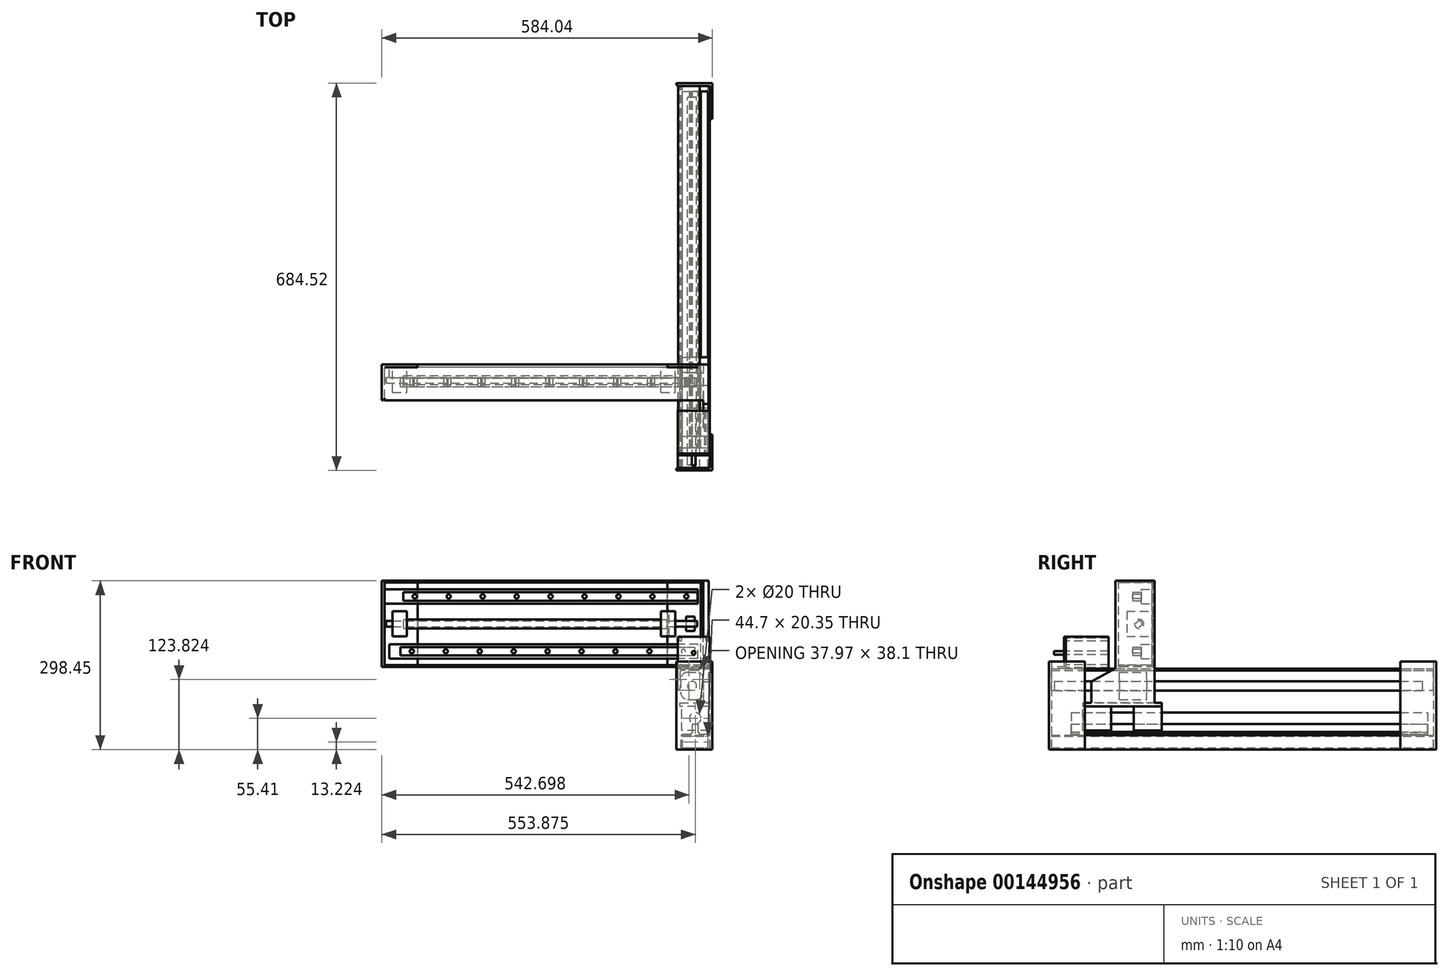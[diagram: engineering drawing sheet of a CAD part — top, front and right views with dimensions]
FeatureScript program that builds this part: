
annotation { "Feature Type Name" : "Feature", "Feature Type Description" : "" }
export const myFeature = defineFeature(function(context is Context, id is Id, definition is map)
    precondition{}
    {
        {
            var Q0;
            Q0=qCreatedBy(makeId("Front.planeOp"),FACE);
            var sketch = newSketch(context, id + "F0", { "sketchPlane" : qUnion([Q0])});
            skLineSegment(sketch, "E0.bottom", {"start": v(200.9, 0) * mm, "end": v(247.7, 0) * mm});
            skLineSegment(sketch, "E0.top", {"start": v(200.9, 25.4) * mm, "end": v(247.7, 25.4) * mm});
            skLineSegment(sketch, "E0.left", {"start": v(198.9, 2) * mm, "end": v(198.9, 23.4) * mm});
            skLineSegment(sketch, "E0.right", {"start": v(249.7, 2) * mm, "end": v(249.7, 23.4) * mm});
            skPoint(sketch, "E1.visualSharp", {"position": v(198.9, 25.4) * mm});
            skArc(sketch, "E1.filletArc", {"start": v(200.9, 25.4) * mm, "mid": v(199.48, 24.81) * mm, "end": v(198.9, 23.4) * mm});
            skPoint(sketch, "E2.visualSharp", {"position": v(198.9, 0) * mm});
            skArc(sketch, "E2.filletArc", {"start": v(198.9, 2) * mm, "mid": v(199.48, 0.59) * mm, "end": v(200.9, 0) * mm});
            skPoint(sketch, "E3.visualSharp", {"position": v(249.7, 25.4) * mm});
            skArc(sketch, "E3.filletArc", {"start": v(249.7, 23.4) * mm, "mid": v(249.1, 24.81) * mm, "end": v(247.7, 25.4) * mm});
            skPoint(sketch, "E4.visualSharp", {"position": v(249.7, 0) * mm});
            skArc(sketch, "E4.filletArc", {"start": v(247.7, 0) * mm, "mid": v(249.1, 0.59) * mm, "end": v(249.7, 2) * mm});
            skLineSegment(sketch, "E5.bottom", {"start": v(201.94, 3.05) * mm, "end": v(246.65, 3.05) * mm});
            skLineSegment(sketch, "E5.top", {"start": v(201.94, 23.4) * mm, "end": v(246.65, 23.4) * mm});
            skLineSegment(sketch, "E5.left", {"start": v(201.94, 3.05) * mm, "end": v(201.94, 23.4) * mm});
            skLineSegment(sketch, "E5.right", {"start": v(246.65, 3.05) * mm, "end": v(246.65, 23.4) * mm});
            skSolve(sketch);
        }
        {
            var Q0;
            Q0=makeQuery(id+"F0.imprint","IMPRINT",FACE,{"disambiguationData":[TD([[makeQuery(id+"F0.imprint","IMPRINT",EDGE,{"derivedFrom":sQuery(id+"F0.wireOp",EDGE,"E0.bottom")}),1.0]])]});
            extrude(context, id + "F1", {"entities" : qUnion([Q0]), "depth" : 675 * mm});
        }
        {
            var Q0;
            Q0=makeQuery(id+"F1.opExtrude","SWEPT_FACE",FACE,{"disambiguationData":[OSD([sQuery(id+"F0.wireOp",EDGE,"E5.bottom")])]});
            var sketch = newSketch(context, id + "F2", { "sketchPlane" : qUnion([Q0])});
            skLineSegment(sketch, "E6", {"start": v(193.96, -675) * mm, "end": v(249.7, -675) * mm});
            skLineSegment(sketch, "E7", {"start": v(249.7, -675) * mm, "end": v(249.7, -619.26) * mm});
            skLineSegment(sketch, "E8", {"start": v(252.7, -616.26) * mm, "end": v(254.46, -616.26) * mm});
            skLineSegment(sketch, "E9", {"start": v(254.46, -616.26) * mm, "end": v(254.46, -679.76) * mm});
            skLineSegment(sketch, "E10", {"start": v(254.46, -679.76) * mm, "end": v(190.96, -679.76) * mm});
            skLineSegment(sketch, "E11", {"start": v(190.96, -679.76) * mm, "end": v(190.96, -678) * mm});
            skPoint(sketch, "E12.visualSharp", {"position": v(190.96, -675) * mm});
            skArc(sketch, "E12.filletArc", {"start": v(193.96, -675) * mm, "mid": v(191.84, -675.88) * mm, "end": v(190.96, -678) * mm});
            skPoint(sketch, "E13.visualSharp", {"position": v(249.7, -616.26) * mm});
            skArc(sketch, "E13.filletArc", {"start": v(252.7, -616.26) * mm, "mid": v(250.57, -617.14) * mm, "end": v(249.7, -619.26) * mm});
            skSolve(sketch);
        }
        {
            var Q0;
            {var subQ0=sQuery(id+"F2.wireOp",EDGE,"E7");Q0=makeQuery(id+"F2.imprint","IMPRINT",FACE,{"disambiguationData":[TD([[makeQuery(id+"F2.imprint","IMPRINT",EDGE,{"derivedFrom":subQ0}),-1.0]])]});}
            extrude(context, id + "F3", {"entities" : qUnion([Q0]), "depth" : 152.4 * mm, "hasSecondDirection" : true, "secondDirectionOppositeDirection" : true, "secondDirectionDepth" : 3.05 * mm});
        }
        {
            var Q0;
            Q0=makeQuery(id+"F1.opExtrude","CAP_FACE",FACE,{"disambiguationData":[OSD([sQuery(id+"F0.wireOp",EDGE,"E0.bottom"),sQuery(id+"F0.wireOp",EDGE,"E0.top"),sQuery(id+"F0.wireOp",EDGE,"E0.left"),sQuery(id+"F0.wireOp",EDGE,"E0.right"),sQuery(id+"F0.wireOp",EDGE,"E1.filletArc"),sQuery(id+"F0.wireOp",EDGE,"E2.filletArc"),sQuery(id+"F0.wireOp",EDGE,"E3.filletArc"),sQuery(id+"F0.wireOp",EDGE,"E4.filletArc"),sQuery(id+"F0.wireOp",EDGE,"E5.bottom"),sQuery(id+"F0.wireOp",EDGE,"E5.top"),sQuery(id+"F0.wireOp",EDGE,"E5.left"),sQuery(id+"F0.wireOp",EDGE,"E5.right")])],"isStart":true});
            var sketch = newSketch(context, id + "F4", { "sketchPlane" : qUnion([Q0])});
            skLineSegment(sketch, "E14", {"start": v(-246.8, 25.4) * mm, "end": v(-201.8, 25.4) * mm});
            skLineSegment(sketch, "E15", {"start": v(-201.8, 25.4) * mm, "end": v(-201.8, 27.4) * mm});
            skLineSegment(sketch, "E16", {"start": v(-201.8, 27.4) * mm, "end": v(-216.8, 27.4) * mm});
            skLineSegment(sketch, "E17", {"start": v(-216.8, 27.4) * mm, "end": v(-219.31, 30.72) * mm});
            skLineSegment(sketch, "E18", {"start": v(-219.31, 30.72) * mm, "end": v(-219.31, 45.4) * mm});
            skLineSegment(sketch, "E19", {"start": v(-219.31, 45.4) * mm, "end": v(-229.31, 45.4) * mm});
            skLineSegment(sketch, "E20", {"start": v(-229.31, 45.4) * mm, "end": v(-229.31, 30.97) * mm});
            skLineSegment(sketch, "E21", {"start": v(-229.31, 30.97) * mm, "end": v(-231.8, 27.4) * mm});
            skLineSegment(sketch, "E22", {"start": v(-231.8, 27.4) * mm, "end": v(-246.8, 27.4) * mm});
            skLineSegment(sketch, "E23", {"start": v(-246.8, 27.4) * mm, "end": v(-246.8, 25.4) * mm});
            skCircle(sketch, "E24", {"center": v(-224.3, 55.41) * mm, "radius": 10 * mm});
            skSolve(sketch);
        }
        {
            var Q0;
            Q0=makeQuery(id+"F4.imprint","IMPRINT",FACE,{"disambiguationData":[TD([[makeQuery(id+"F4.imprint","IMPRINT",EDGE,{"derivedFrom":sQuery(id+"F4.wireOp",EDGE,"E24")}),1.0]])]});
            var Q1;
            Q1=makeQuery(id+"F4.imprint","IMPRINT",FACE,{"disambiguationData":[TD([[makeQuery(id+"F4.imprint","IMPRINT",EDGE,{"derivedFrom":sQuery(id+"F4.wireOp",EDGE,"E14")}),-1.0]])]});
            extrude(context, id + "F5", {"entities" : qUnion([Q0, Q1]), "oppositeDirection" : true, "depth" : 640 * mm, "hasSecondDirection" : true, "secondDirectionOppositeDirection" : true, "secondDirectionDepth" : 10 * mm});
        }
        {
            var Q0;
            Q0=makeQuery(id+"F1.opExtrude","SWEPT_FACE",FACE,{"disambiguationData":[OSD([sQuery(id+"F0.wireOp",EDGE,"E5.bottom")])]});
            var sketch = newSketch(context, id + "F6", { "sketchPlane" : qUnion([Q0])});
            skLineSegment(sketch, "E25", {"start": v(194, 0) * mm, "end": v(249.7, 0) * mm});
            skLineSegment(sketch, "E26", {"start": v(249.7, 0) * mm, "end": v(249.7, -55.74) * mm});
            skLineSegment(sketch, "E27", {"start": v(252.7, -58.74) * mm, "end": v(254.46, -58.74) * mm});
            skLineSegment(sketch, "E28", {"start": v(254.46, -58.74) * mm, "end": v(254.46, 4.76) * mm});
            skLineSegment(sketch, "E29", {"start": v(254.46, 4.76) * mm, "end": v(190.96, 4.76) * mm});
            skLineSegment(sketch, "E30", {"start": v(190.96, 4.76) * mm, "end": v(191, 2.93) * mm});
            skPoint(sketch, "E31.visualSharp", {"position": v(191.08, 0) * mm});
            skArc(sketch, "E31.filletArc", {"start": v(191, 2.93) * mm, "mid": v(191.9, 0.85) * mm, "end": v(194, 0) * mm});
            skPoint(sketch, "E32.visualSharp", {"position": v(249.7, -58.74) * mm});
            skArc(sketch, "E32.filletArc", {"start": v(249.7, -55.74) * mm, "mid": v(250.57, -57.86) * mm, "end": v(252.7, -58.74) * mm});
            skSolve(sketch);
        }
        {
            var Q0;
            {var subQ0=sQuery(id+"F6.wireOp",EDGE,"E26");Q0=makeQuery(id+"F6.imprint","IMPRINT",FACE,{"disambiguationData":[TD([[makeQuery(id+"F6.imprint","IMPRINT",EDGE,{"derivedFrom":subQ0}),1.0]])]});}
            extrude(context, id + "F7", {"entities" : qUnion([Q0]), "depth" : 152.4 * mm, "hasSecondDirection" : true, "secondDirectionOppositeDirection" : true, "secondDirectionDepth" : 3.05 * mm});
        }
        {
            var Q0;
            Q0=makeQuery(id+"F7.opExtrude","SWEPT_FACE",FACE,{"disambiguationData":[OSD([sQuery(id+"F6.wireOp",EDGE,"E25")])]});
            var sketch = newSketch(context, id + "F8", { "sketchPlane" : qUnion([Q0])});
            skLineSegment(sketch, "E33", {"start": v(194, 142.88) * mm, "end": v(232.1, 142.88) * mm});
            skLineSegment(sketch, "E34", {"start": v(232.1, 142.88) * mm, "end": v(232.1, 142.7) * mm});
            skLineSegment(sketch, "E35", {"start": v(229.1, 139.7) * mm, "end": v(200.3, 139.7) * mm});
            skLineSegment(sketch, "E36", {"start": v(194.13, 104.77) * mm, "end": v(194.13, 142.88) * mm});
            skPoint(sketch, "E37.visualSharp", {"position": v(232.1, 139.7) * mm});
            skArc(sketch, "E37.filletArc", {"start": v(229.1, 139.7) * mm, "mid": v(231.22, 140.58) * mm, "end": v(232.1, 142.7) * mm});
            skLineSegment(sketch, "E38", {"start": v(197.3, 136.7) * mm, "end": v(197.3, 107.77) * mm});
            skLineSegment(sketch, "E39", {"start": v(194.24, 104.77) * mm, "end": v(194.13, 104.77) * mm});
            skPoint(sketch, "E40.visualSharp", {"position": v(197.3, 139.7) * mm});
            skArc(sketch, "E40.filletArc", {"start": v(200.3, 139.7) * mm, "mid": v(198.19, 138.82) * mm, "end": v(197.3, 136.7) * mm});
            skPoint(sketch, "E41.visualSharp", {"position": v(197.3, 104.7) * mm});
            skArc(sketch, "E41.filletArc", {"start": v(194.24, 104.77) * mm, "mid": v(196.4, 105.63) * mm, "end": v(197.3, 107.77) * mm});
            skSolve(sketch);
        }
        {
            var Q0;
            Q0=makeQuery(id+"F8.imprint","IMPRINT",FACE,{"disambiguationData":[TD([[makeQuery(id+"F8.imprint","IMPRINT",EDGE,{"derivedFrom":sQuery(id+"F8.wireOp",EDGE,"E33")}),-1.0]])]});
            extrude(context, id + "F9", {"entities" : qUnion([Q0]), "operationType" : NewBodyOperationType.ADD, "depth" : 675 * mm});
        }
        {
            var Q0;
            Q0=makeQuery(id+"F5.opExtrude","CAP_FACE",FACE,{"disambiguationData":[OSD([sQuery(id+"F4.wireOp",EDGE,"E24")])],"isStart":true});
            var sketch = newSketch(context, id + "F10", { "sketchPlane" : qUnion([Q0])});
            skLineSegment(sketch, "E42.bottom", {"start": v(-248.3, 33.48) * mm, "end": v(-200.3, 33.48) * mm});
            skLineSegment(sketch, "E42.top", {"start": v(-248.3, 76.2) * mm, "end": v(-200.3, 76.2) * mm});
            skLineSegment(sketch, "E42.left", {"start": v(-248.3, 33.48) * mm, "end": v(-248.3, 76.2) * mm});
            skLineSegment(sketch, "E42.right", {"start": v(-200.3, 33.48) * mm, "end": v(-200.3, 76.2) * mm});
            skLineSegment(sketch, "E43", {"start": v(-248.3, 76.2) * mm, "end": v(-197.5, 76.2) * mm});
            skLineSegment(sketch, "E44", {"start": v(-197.5, 76.2) * mm, "end": v(-197.5, 82.55) * mm});
            skLineSegment(sketch, "E45", {"start": v(-197.5, 82.55) * mm, "end": v(-248.3, 82.55) * mm});
            skLineSegment(sketch, "E46", {"start": v(-248.3, 82.55) * mm, "end": v(-248.3, 76.2) * mm});
            skCircle(sketch, "E47", {"center": v(-218.77, 112.55) * mm, "radius": 8 * mm});
            skLineSegment(sketch, "E48.bottom", {"start": v(-210.77, 136.55) * mm, "end": v(-226.77, 136.55) * mm});
            skLineSegment(sketch, "E48.top", {"start": v(-210.77, 88.55) * mm, "end": v(-226.77, 88.55) * mm});
            skLineSegment(sketch, "E48.left", {"start": v(-198.77, 124.55) * mm, "end": v(-198.77, 100.55) * mm});
            skLineSegment(sketch, "E48.right", {"start": v(-238.77, 124.55) * mm, "end": v(-238.77, 100.55) * mm});
            skPoint(sketch, "E49.visualSharp", {"position": v(-198.77, 136.55) * mm});
            skArc(sketch, "E49.filletArc", {"start": v(-198.77, 124.55) * mm, "mid": v(-202.28, 133.03) * mm, "end": v(-210.77, 136.55) * mm});
            skPoint(sketch, "E50.visualSharp", {"position": v(-198.77, 88.55) * mm});
            skArc(sketch, "E50.filletArc", {"start": v(-210.77, 88.55) * mm, "mid": v(-202.28, 92.06) * mm, "end": v(-198.77, 100.55) * mm});
            skPoint(sketch, "E51.visualSharp", {"position": v(-238.77, 88.55) * mm});
            skArc(sketch, "E51.filletArc", {"start": v(-238.77, 100.55) * mm, "mid": v(-235.26, 92.06) * mm, "end": v(-226.77, 88.55) * mm});
            skPoint(sketch, "E52.visualSharp", {"position": v(-238.77, 136.55) * mm});
            skArc(sketch, "E52.filletArc", {"start": v(-226.77, 136.55) * mm, "mid": v(-235.26, 133.03) * mm, "end": v(-238.77, 124.55) * mm});
            skSolve(sketch);
        }
        {
            var Q0;
            Q0=makeQuery(id+"F10.imprint","IMPRINT",FACE,{"disambiguationData":[TD([[makeQuery(id+"F10.imprint","IMPRINT",EDGE,{"derivedFrom":sQuery(id+"F10.wireOp",EDGE,"E42.bottom")}),1.0]])]});
            extrude(context, id + "F11", {"entities" : qUnion([Q0]), "oppositeDirection" : true, "depth" : 520 * mm, "hasSecondDirection" : true, "secondDirectionOppositeDirection" : true, "secondDirectionDepth" : 470 * mm});
        }
        {
            var Q0;
            Q0=makeQuery(id+"F11.opExtrude","CAP_FACE",FACE,{"disambiguationData":[OSD([sQuery(id+"F4.wireOp",EDGE,"E24"),sQuery(id+"F10.wireOp",EDGE,"E42.bottom"),sQuery(id+"F10.wireOp",EDGE,"E42.left"),sQuery(id+"F10.wireOp",EDGE,"E42.right"),sQuery(id+"F10.wireOp",EDGE,"E43")])],"isStart":true});
            extrude(context, id + "F12", {"entities" : qUnion([Q0]), "oppositeDirection" : true, "depth" : 139.7 * mm, "hasSecondDirection" : true, "secondDirectionOppositeDirection" : true, "secondDirectionDepth" : 89.7 * mm});
        }
        {
            var Q0;
            {var subQ0=sQuery(id+"F10.wireOp",EDGE,"E44");Q0=makeQuery(id+"F10.imprint","IMPRINT",FACE,{"disambiguationData":[TD([[makeQuery(id+"F10.imprint","IMPRINT",EDGE,{"derivedFrom":subQ0}),1.0]])]});}
            extrude(context, id + "F13", {"entities" : qUnion([Q0]), "oppositeDirection" : true, "depth" : 609.7 * mm, "hasSecondDirection" : true, "secondDirectionOppositeDirection" : true, "secondDirectionDepth" : 470 * mm});
        }
        {
            var Q0;
            Q0=makeQuery(id+"F13.opExtrude","SWEPT_FACE",FACE,{"disambiguationData":[OSD([sQuery(id+"F10.wireOp",EDGE,"E45")])]});
            var sketch = newSketch(context, id + "F14", { "sketchPlane" : qUnion([Q0])});
            skLineSegment(sketch, "E53.bottom", {"start": v(248.3, -492.7) * mm, "end": v(238.77, -492.7) * mm});
            skLineSegment(sketch, "E53.top", {"start": v(248.3, -604.7) * mm, "end": v(238.77, -604.7) * mm});
            skLineSegment(sketch, "E53.left", {"start": v(248.3, -492.7) * mm, "end": v(248.3, -604.7) * mm});
            skLineSegment(sketch, "E53.right", {"start": v(238.77, -492.7) * mm, "end": v(238.77, -604.7) * mm});
            skSolve(sketch);
        }
        {
            var Q0;
            Q0=makeQuery(id+"F14.imprint","IMPRINT",FACE,{"disambiguationData":[TD([[makeQuery(id+"F14.imprint","IMPRINT",EDGE,{"derivedFrom":sQuery(id+"F14.wireOp",EDGE,"E53.bottom")}),1.0]])]});
            extrude(context, id + "F15", {"entities" : qUnion([Q0]), "operationType" : NewBodyOperationType.ADD, "depth" : 215.9 * mm});
        }
        {
            var Q0;
            Q0=makeQuery(id+"F10.imprint","IMPRINT",FACE,{"disambiguationData":[TD([[makeQuery(id+"F10.imprint","IMPRINT",EDGE,{"derivedFrom":sQuery(id+"F10.wireOp",EDGE,"E47")}),1.0]])]});
            extrude(context, id + "F16", {"entities" : qUnion([Q0]), "oppositeDirection" : true, "depth" : 660 * mm, "hasSecondDirection" : true, "secondDirectionOppositeDirection" : true, "secondDirectionDepth" : 10 * mm});
        }
        {
            var Q0;
            Q0=makeQuery(id+"F10.imprint","IMPRINT",FACE,{"disambiguationData":[TD([[makeQuery(id+"F10.imprint","IMPRINT",EDGE,{"derivedFrom":sQuery(id+"F10.wireOp",EDGE,"E47")}),-1.0]])]});
            extrude(context, id + "F17", {"entities" : qUnion([Q0]), "oppositeDirection" : true, "depth" : 545 * mm, "hasSecondDirection" : true, "secondDirectionOppositeDirection" : true, "secondDirectionDepth" : 497 * mm});
        }
        {
            var Q0;
            Q0=makeQuery(id+"F15.boolean.opBoolean","MERGE",FACE,{"derivedFrom":[makeQuery(id+"F13.opExtrude","SWEPT_FACE",FACE,{"disambiguationData":[OSD([sQuery(id+"F10.wireOp",EDGE,"E46")])]}),makeQuery(id+"F15.opExtrude","SWEPT_FACE",FACE,{"disambiguationData":[OSD([sQuery(id+"F14.wireOp",EDGE,"E53.left")])]})]});
            var sketch = newSketch(context, id + "F18", { "sketchPlane" : qUnion([Q0])});
            skLineSegment(sketch, "E54", {"start": v(-604.7, 119.94) * mm, "end": v(-562.4, 143.7) * mm});
            skLineSegment(sketch, "E55", {"start": v(-562.4, 143.7) * mm, "end": v(-562.4, 298.45) * mm});
            skLineSegment(sketch, "E56", {"start": v(-562.4, 298.45) * mm, "end": v(-604.7, 298.45) * mm});
            skLineSegment(sketch, "E57", {"start": v(-604.7, 298.45) * mm, "end": v(-604.7, 119.94) * mm});
            skSolve(sketch);
        }
        {
            var Q0;
            Q0 = qSketchRegion(id + "F18", true);
            extrude(context, id + "F19", {"entities" : qUnion([Q0]), "operationType" : NewBodyOperationType.REMOVE, "oppositeDirection" : true, "depth" : 9.53 * mm});
        }
        {
            var Q0;
            Q0=makeQuery(id+"F9.opExtrude","SWEPT_FACE",FACE,{"disambiguationData":[OSD([sQuery(id+"F8.wireOp",EDGE,"E33")])]});
            var sketch = newSketch(context, id + "F20", { "sketchPlane" : qUnion([Q0])});
            skLineSegment(sketch, "E58.bottom", {"start": v(193.3, -650) * mm, "end": v(249.7, -650) * mm});
            skLineSegment(sketch, "E58.top", {"start": v(193.3, -675) * mm, "end": v(249.7, -675) * mm});
            skLineSegment(sketch, "E58.left", {"start": v(193.3, -650) * mm, "end": v(193.3, -675) * mm});
            skLineSegment(sketch, "E58.right", {"start": v(249.7, -650) * mm, "end": v(249.7, -675) * mm});
            skSolve(sketch);
        }
        {
            var Q0;
            Q0 = qSketchRegion(id + "F20", true);
            extrude(context, id + "F21", {"entities" : qUnion([Q0]), "depth" : 3.17 * mm});
        }
        {
            var Q0;
            Q0=makeQuery(id+"F21.opExtrude","CAP_FACE",FACE,{"disambiguationData":[OSD([sQuery(id+"F20.wireOp",EDGE,"E58.bottom"),sQuery(id+"F20.wireOp",EDGE,"E58.top"),sQuery(id+"F20.wireOp",EDGE,"E58.left"),sQuery(id+"F20.wireOp",EDGE,"E58.right")])],"isStart":false});
            var sketch = newSketch(context, id + "F22", { "sketchPlane" : qUnion([Q0])});
            skLineSegment(sketch, "E59.bottom", {"start": v(193.3, -650) * mm, "end": v(249.7, -650) * mm});
            skLineSegment(sketch, "E59.top", {"start": v(193.3, -653.18) * mm, "end": v(249.7, -653.18) * mm});
            skLineSegment(sketch, "E59.left", {"start": v(193.3, -650) * mm, "end": v(193.3, -653.18) * mm});
            skLineSegment(sketch, "E59.right", {"start": v(249.7, -650) * mm, "end": v(249.7, -653.18) * mm});
            skSolve(sketch);
        }
        {
            var Q0;
            Q0 = qSketchRegion(id + "F22", true);
            extrude(context, id + "F23", {"entities" : qUnion([Q0]), "depth" : 53.23 * mm});
        }
        {
            var Q0;
            Q0=makeQuery(id+"F23.opExtrude","SWEPT_FACE",FACE,{"disambiguationData":[OSD([sQuery(id+"F22.wireOp",EDGE,"E59.bottom")])]});
            var sketch = newSketch(context, id + "F24", { "sketchPlane" : qUnion([Q0])});
            skCircle(sketch, "E60", {"center": v(-221.5, 171.08) * mm, "radius": 3.17 * mm});
            skLineSegment(sketch, "E61.bottom", {"start": v(-244.7, 199.28) * mm, "end": v(-198.3, 199.28) * mm});
            skLineSegment(sketch, "E61.top", {"start": v(-244.7, 142.88) * mm, "end": v(-198.3, 142.88) * mm});
            skLineSegment(sketch, "E61.left", {"start": v(-249.7, 194.28) * mm, "end": v(-249.7, 147.88) * mm});
            skLineSegment(sketch, "E61.right", {"start": v(-193.3, 194.28) * mm, "end": v(-193.3, 147.88) * mm});
            skPoint(sketch, "E62.visualSharp", {"position": v(-249.7, 142.88) * mm});
            skArc(sketch, "E62.filletArc", {"start": v(-249.7, 147.88) * mm, "mid": v(-248.23, 144.34) * mm, "end": v(-244.7, 142.87) * mm});
            skPoint(sketch, "E63.visualSharp", {"position": v(-193.3, 142.88) * mm});
            skArc(sketch, "E63.filletArc", {"start": v(-198.3, 142.87) * mm, "mid": v(-194.76, 144.34) * mm, "end": v(-193.3, 147.88) * mm});
            skPoint(sketch, "E64.visualSharp", {"position": v(-249.7, 199.28) * mm});
            skArc(sketch, "E64.filletArc", {"start": v(-244.7, 199.28) * mm, "mid": v(-248.23, 197.81) * mm, "end": v(-249.7, 194.28) * mm});
            skPoint(sketch, "E65.visualSharp", {"position": v(-193.3, 199.28) * mm});
            skArc(sketch, "E65.filletArc", {"start": v(-193.3, 194.28) * mm, "mid": v(-194.76, 197.81) * mm, "end": v(-198.3, 199.28) * mm});
            skCircle(sketch, "E66", {"center": v(-197.92, 194.65) * mm, "radius": 2.55 * mm});
            skCircle(sketch, "E67", {"center": v(-197.92, 147.5) * mm, "radius": 2.55 * mm});
            skCircle(sketch, "E68", {"center": v(-245.06, 194.65) * mm, "radius": 2.55 * mm});
            skCircle(sketch, "E69", {"center": v(-243.2, 147.5) * mm, "radius": 2.55 * mm});
            skSolve(sketch);
        }
        {
            var Q0;
            Q0=makeQuery(id+"F24.imprint","IMPRINT",FACE,{"disambiguationData":[TD([[makeQuery(id+"F24.imprint","IMPRINT",EDGE,{"derivedFrom":sQuery(id+"F24.wireOp",EDGE,"E60")}),1.0]])]});
            extrude(context, id + "F25", {"entities" : qUnion([Q0]), "operationType" : NewBodyOperationType.ADD, "oppositeDirection" : true, "depth" : 21 * mm});
        }
        {
            var Q0;
            Q0 = qSketchRegion(id + "F24", true);
            extrude(context, id + "F26", {"entities" : qUnion([Q0]), "depth" : 76 * mm});
        }
        {
            var Q0;
            Q0=makeQuery(id+"F15.opExtrude","CAP_FACE",FACE,{"disambiguationData":[OSD([sQuery(id+"F14.wireOp",EDGE,"E53.bottom"),sQuery(id+"F14.wireOp",EDGE,"E53.top"),sQuery(id+"F14.wireOp",EDGE,"E53.left"),sQuery(id+"F14.wireOp",EDGE,"E53.right")])],"isStart":false});
            var sketch = newSketch(context, id + "F27", { "sketchPlane" : qUnion([Q0])});
            skLineSegment(sketch, "E70", {"start": v(238.77, -492.7) * mm, "end": v(238.77, -556.2) * mm});
            skLineSegment(sketch, "E71", {"start": v(238.77, -556.2) * mm, "end": v(236.76, -556.2) * mm});
            skLineSegment(sketch, "E72", {"start": v(234, -553.45) * mm, "end": v(234, -502.46) * mm});
            skLineSegment(sketch, "E73", {"start": v(229, -497.46) * mm, "end": v(178.2, -497.46) * mm});
            skLineSegment(sketch, "E74", {"start": v(175.27, -494.53) * mm, "end": v(175.27, -492.7) * mm});
            skLineSegment(sketch, "E75", {"start": v(175.27, -492.7) * mm, "end": v(238.77, -492.7) * mm});
            skPoint(sketch, "E76.visualSharp", {"position": v(234, -497.46) * mm});
            skArc(sketch, "E76.filletArc", {"start": v(234, -502.46) * mm, "mid": v(232.54, -498.93) * mm, "end": v(229, -497.46) * mm});
            skPoint(sketch, "E77.visualSharp", {"position": v(175.27, -497.46) * mm});
            skArc(sketch, "E77.filletArc", {"start": v(175.27, -494.53) * mm, "mid": v(176.13, -496.6) * mm, "end": v(178.2, -497.46) * mm});
            skPoint(sketch, "E78.visualSharp", {"position": v(234, -556.2) * mm});
            skArc(sketch, "E78.filletArc", {"start": v(234, -553.45) * mm, "mid": v(234.81, -555.4) * mm, "end": v(236.76, -556.2) * mm});
            skSolve(sketch);
        }
        {
            var Q0;
            Q0=makeQuery(id+"F27.imprint","IMPRINT",FACE,{"disambiguationData":[TD([[makeQuery(id+"F27.imprint","IMPRINT",EDGE,{"derivedFrom":sQuery(id+"F27.wireOp",EDGE,"E70")}),-1.0]])]});
            extrude(context, id + "F28", {"entities" : qUnion([Q0]), "operationType" : NewBodyOperationType.ADD, "oppositeDirection" : true, "depth" : 152.4 * mm});
        }
        {
            var Q0;
            Q0=makeQuery(id+"F28.opExtrude","SWEPT_FACE",FACE,{"disambiguationData":[OSD([sQuery(id+"F27.wireOp",EDGE,"E74")])]});
            var sketch = newSketch(context, id + "F29", { "sketchPlane" : qUnion([Q0])});
            skLineSegment(sketch, "E79.bottom", {"start": v(492.7, 298.45) * mm, "end": v(497.46, 298.45) * mm});
            skLineSegment(sketch, "E79.top", {"start": v(492.7, 146.05) * mm, "end": v(497.46, 146.05) * mm});
            skLineSegment(sketch, "E79.left", {"start": v(492.7, 298.45) * mm, "end": v(492.7, 146.05) * mm});
            skLineSegment(sketch, "E79.right", {"start": v(497.46, 298.45) * mm, "end": v(497.46, 146.05) * mm});
            skSolve(sketch);
        }
        {
            var Q0;
            Q0 = qSketchRegion(id + "F29", true);
            extrude(context, id + "F30", {"entities" : qUnion([Q0]), "operationType" : NewBodyOperationType.ADD, "depth" : 441.35 * mm});
        }
        {
            var Q0;
            Q0=makeQuery(id+"F30.boolean.opBoolean","MERGE",FACE,{"derivedFrom":[makeQuery(id+"F28.boolean.opBoolean","MERGE",FACE,{"derivedFrom":[makeQuery(id+"F15.opExtrude","CAP_FACE",FACE,{"disambiguationData":[OSD([sQuery(id+"F14.wireOp",EDGE,"E53.bottom"),sQuery(id+"F14.wireOp",EDGE,"E53.top"),sQuery(id+"F14.wireOp",EDGE,"E53.left"),sQuery(id+"F14.wireOp",EDGE,"E53.right")])],"isStart":false}),makeQuery(id+"F28.opExtrude","CAP_FACE",FACE,{"disambiguationData":[OSD([sQuery(id+"F27.wireOp",EDGE,"E70"),sQuery(id+"F27.wireOp",EDGE,"E71"),sQuery(id+"F27.wireOp",EDGE,"E72"),sQuery(id+"F27.wireOp",EDGE,"E73"),sQuery(id+"F27.wireOp",EDGE,"E74"),sQuery(id+"F27.wireOp",EDGE,"E75"),sQuery(id+"F27.wireOp",EDGE,"E76.filletArc"),sQuery(id+"F27.wireOp",EDGE,"E77.filletArc"),sQuery(id+"F27.wireOp",EDGE,"E78.filletArc")])],"isStart":true})]}),makeQuery(id+"F30.opExtrude","SWEPT_FACE",FACE,{"disambiguationData":[OSD([sQuery(id+"F29.wireOp",EDGE,"E79.bottom")])]})]});
            var sketch = newSketch(context, id + "F31", { "sketchPlane" : qUnion([Q0])});
            skLineSegment(sketch, "E80", {"start": v(-266.08, -492.7) * mm, "end": v(-329.58, -492.7) * mm});
            skLineSegment(sketch, "E81", {"start": v(-329.58, -492.7) * mm, "end": v(-329.58, -556.2) * mm});
            skLineSegment(sketch, "E82", {"start": v(-329.58, -556.2) * mm, "end": v(-329.16, -556.2) * mm});
            skLineSegment(sketch, "E83", {"start": v(-324.82, -551.86) * mm, "end": v(-324.82, -500.21) * mm});
            skLineSegment(sketch, "E84", {"start": v(-322.07, -497.46) * mm, "end": v(-270.07, -497.46) * mm});
            skLineSegment(sketch, "E85", {"start": v(-266.08, -493.47) * mm, "end": v(-266.08, -492.7) * mm});
            skPoint(sketch, "E86.visualSharp", {"position": v(-324.82, -497.46) * mm});
            skArc(sketch, "E86.filletArc", {"start": v(-322.07, -497.46) * mm, "mid": v(-324.01, -498.27) * mm, "end": v(-324.82, -500.21) * mm});
            skPoint(sketch, "E87.visualSharp", {"position": v(-266.08, -497.46) * mm});
            skArc(sketch, "E87.filletArc", {"start": v(-270.07, -497.46) * mm, "mid": v(-267.25, -496.3) * mm, "end": v(-266.08, -493.47) * mm});
            skPoint(sketch, "E88.visualSharp", {"position": v(-324.82, -556.2) * mm});
            skArc(sketch, "E88.filletArc", {"start": v(-329.16, -556.2) * mm, "mid": v(-326.09, -554.93) * mm, "end": v(-324.82, -551.86) * mm});
            skSolve(sketch);
        }
        {
            var Q0;
            Q0=makeQuery(id+"F31.imprint","IMPRINT",FACE,{"disambiguationData":[TD([[makeQuery(id+"F31.imprint","IMPRINT",EDGE,{"derivedFrom":sQuery(id+"F31.wireOp",EDGE,"E80")}),1.0]])]});
            extrude(context, id + "F32", {"entities" : qUnion([Q0]), "operationType" : NewBodyOperationType.ADD, "oppositeDirection" : true, "depth" : 152.4 * mm});
        }
        {
            var Q0;
            Q0=makeQuery(id+"F28.opExtrude","SWEPT_FACE",FACE,{"disambiguationData":[OSD([sQuery(id+"F27.wireOp",EDGE,"E73")])]});
            var sketch = newSketch(context, id + "F33", { "sketchPlane" : qUnion([Q0])});
            skLineSegment(sketch, "E89.bottom", {"start": v(234, 283.45) * mm, "end": v(-324.82, 283.45) * mm});
            skLineSegment(sketch, "E89.top", {"start": v(234, 258.05) * mm, "end": v(-324.82, 258.05) * mm});
            skLineSegment(sketch, "E89.left", {"start": v(234, 283.45) * mm, "end": v(234, 258.05) * mm});
            skLineSegment(sketch, "E89.right", {"start": v(-324.82, 283.45) * mm, "end": v(-324.82, 258.05) * mm});
            skLineSegment(sketch, "E90.bottom", {"start": v(233.5, 186.45) * mm, "end": v(-316.5, 186.45) * mm});
            skLineSegment(sketch, "E90.top", {"start": v(233.5, 161.05) * mm, "end": v(-316.5, 161.05) * mm});
            skLineSegment(sketch, "E90.left", {"start": v(233.5, 186.45) * mm, "end": v(233.5, 161.05) * mm});
            skLineSegment(sketch, "E90.right", {"start": v(-316.5, 186.45) * mm, "end": v(-316.5, 161.05) * mm});
            skSolve(sketch);
        }
        {
            var Q0;
            {var subQ0=sQuery(id+"F33.wireOp",EDGE,"E89.right");Q0=makeQuery(id+"F33.imprint","IMPRINT",FACE,{"disambiguationData":[TD([[makeQuery(id+"F33.imprint","IMPRINT",EDGE,{"derivedFrom":subQ0}),1.0]])]});}
            var Q1;
            {var subQ0=sQuery(id+"F33.wireOp",EDGE,"E89.bottom");var subQ1=sQuery(id+"F27.wireOp",EDGE,"E73");var subQ2=makeQuery(id+"F28.opExtrude","SWEPT_EDGE",EDGE,{"disambiguationData":[OSD([subQ1,sQuery(id+"F27.wireOp",EDGE,"E76.filletArc")])]});var subQ3=makeQuery(id+"F33.imprint","INTERSECT",VERTEX,{"derivedFrom":[subQ2,subQ0]});Q1=makeQuery(id+"F33.imprint","IMPRINT",FACE,{"disambiguationData":[TD([[makeQuery(id+"F33.imprint","IMPRINT",EDGE,{"disambiguationData":[TD([[subQ3,-1.0]])],"derivedFrom":subQ0}),1.0]])]});}
            var Q2;
            {var subQ0=sQuery(id+"F33.wireOp",EDGE,"E90.bottom");var subQ1=sQuery(id+"F27.wireOp",EDGE,"E73");var subQ2=makeQuery(id+"F28.opExtrude","SWEPT_EDGE",EDGE,{"disambiguationData":[OSD([subQ1,sQuery(id+"F27.wireOp",EDGE,"E76.filletArc")])]});var subQ3=makeQuery(id+"F33.imprint","INTERSECT",VERTEX,{"derivedFrom":[subQ2,subQ0]});Q2=makeQuery(id+"F33.imprint","IMPRINT",FACE,{"disambiguationData":[TD([[makeQuery(id+"F33.imprint","IMPRINT",EDGE,{"disambiguationData":[TD([[subQ3,-1.0]])],"derivedFrom":subQ0}),1.0]])]});}
            var Q3;
            {var subQ0=sQuery(id+"F33.wireOp",EDGE,"E90.right");Q3=makeQuery(id+"F33.imprint","IMPRINT",FACE,{"disambiguationData":[TD([[makeQuery(id+"F33.imprint","IMPRINT",EDGE,{"derivedFrom":subQ0}),1.0]])]});}
            extrude(context, id + "F34", {"entities" : qUnion([Q0, Q1, Q2, Q3]), "depth" : 19.05 * mm});
        }
        {
            var Q0;
            Q0=makeQuery(id+"F34.opExtrude","CAP_FACE",FACE,{"disambiguationData":[OSD([sQuery(id+"F27.wireOp",EDGE,"E73"),sQuery(id+"F27.wireOp",EDGE,"E76.filletArc"),sQuery(id+"F33.wireOp",EDGE,"E89.bottom"),sQuery(id+"F33.wireOp",EDGE,"E89.top"),sQuery(id+"F33.wireOp",EDGE,"E89.right")])],"isStart":false});
            var sketch = newSketch(context, id + "F35", { "sketchPlane" : qUnion([Q0])});
            skLineSegment(sketch, "E91.bottom", {"start": v(-291.4, 278.25) * mm, "end": v(228.6, 278.25) * mm});
            skLineSegment(sketch, "E91.top", {"start": v(-291.4, 263.25) * mm, "end": v(228.6, 263.25) * mm});
            skLineSegment(sketch, "E91.left", {"start": v(-291.4, 278.25) * mm, "end": v(-291.4, 263.25) * mm});
            skLineSegment(sketch, "E91.right", {"start": v(228.6, 278.25) * mm, "end": v(228.6, 263.25) * mm});
            skLineSegment(sketch, "E92.bottom", {"start": v(-296.63, 181.25) * mm, "end": v(223.37, 181.25) * mm});
            skLineSegment(sketch, "E92.top", {"start": v(-296.63, 166.25) * mm, "end": v(223.37, 166.25) * mm});
            skLineSegment(sketch, "E92.left", {"start": v(-296.63, 181.25) * mm, "end": v(-296.63, 166.25) * mm});
            skLineSegment(sketch, "E92.right", {"start": v(223.37, 181.25) * mm, "end": v(223.37, 166.25) * mm});
            skSolve(sketch);
        }
        {
            var Q0;
            Q0=makeQuery(id+"F35.imprint","IMPRINT",FACE,{"disambiguationData":[TD([[makeQuery(id+"F35.imprint","IMPRINT",EDGE,{"derivedFrom":sQuery(id+"F35.wireOp",EDGE,"E91.bottom")}),-1.0]])]});
            var Q1;
            Q1=makeQuery(id+"F35.imprint","IMPRINT",FACE,{"disambiguationData":[TD([[makeQuery(id+"F35.imprint","IMPRINT",EDGE,{"derivedFrom":sQuery(id+"F35.wireOp",EDGE,"E92.bottom")}),-1.0]])]});
            extrude(context, id + "F36", {"entities" : qUnion([Q0, Q1]), "operationType" : NewBodyOperationType.ADD, "depth" : 15 * mm, "offsetDistance" : 25 * mm});
        }
        {
            var Q0;
            Q0=makeQuery(id+"F36.opExtrude","CAP_FACE",FACE,{"disambiguationData":[OSD([sQuery(id+"F35.wireOp",EDGE,"E91.bottom"),sQuery(id+"F35.wireOp",EDGE,"E91.top"),sQuery(id+"F35.wireOp",EDGE,"E91.left"),sQuery(id+"F35.wireOp",EDGE,"E91.right")])],"isStart":false});
            var sketch = newSketch(context, id + "F37", { "sketchPlane" : qUnion([Q0])});
            skCircle(sketch, "E93", {"center": v(-271.4, 270.75) * mm, "radius": 3.75 * mm});
            skCircle(sketch, "E94", {"center": v(-211.4, 270.75) * mm, "radius": 3.75 * mm});
            skCircle(sketch, "E95", {"center": v(-151.4, 270.75) * mm, "radius": 3.75 * mm});
            skCircle(sketch, "E96", {"center": v(-91.4, 270.75) * mm, "radius": 3.75 * mm});
            skCircle(sketch, "E97", {"center": v(-31.4, 270.75) * mm, "radius": 3.75 * mm});
            skCircle(sketch, "E98", {"center": v(28.6, 270.75) * mm, "radius": 3.75 * mm});
            skCircle(sketch, "E99", {"center": v(88.6, 270.75) * mm, "radius": 3.75 * mm});
            skCircle(sketch, "E100", {"center": v(148.6, 270.75) * mm, "radius": 3.75 * mm});
            skCircle(sketch, "E101", {"center": v(208.6, 270.75) * mm, "radius": 3.75 * mm});
            skCircle(sketch, "E102", {"center": v(-276.63, 173.75) * mm, "radius": 3.75 * mm});
            skCircle(sketch, "E103", {"center": v(-216.63, 173.75) * mm, "radius": 3.75 * mm});
            skCircle(sketch, "E104", {"center": v(-156.63, 173.75) * mm, "radius": 3.75 * mm});
            skCircle(sketch, "E105", {"center": v(-96.63, 173.75) * mm, "radius": 3.75 * mm});
            skCircle(sketch, "E106", {"center": v(-36.63, 173.75) * mm, "radius": 3.75 * mm});
            skCircle(sketch, "E107", {"center": v(23.37, 173.75) * mm, "radius": 3.75 * mm});
            skCircle(sketch, "E108", {"center": v(83.37, 173.75) * mm, "radius": 3.75 * mm});
            skCircle(sketch, "E109", {"center": v(143.37, 173.75) * mm, "radius": 3.75 * mm});
            skCircle(sketch, "E110", {"center": v(203.37, 173.75) * mm, "radius": 3.75 * mm});
            skSolve(sketch);
        }
        {
            var Q0;
            Q0=makeQuery(id+"F37.imprint","IMPRINT",FACE,{"disambiguationData":[TD([[makeQuery(id+"F37.imprint","IMPRINT",EDGE,{"derivedFrom":sQuery(id+"F37.wireOp",EDGE,"E93")}),1.0]])]});
            var Q1;
            Q1=makeQuery(id+"F37.imprint","IMPRINT",FACE,{"disambiguationData":[TD([[makeQuery(id+"F37.imprint","IMPRINT",EDGE,{"derivedFrom":sQuery(id+"F37.wireOp",EDGE,"E94")}),1.0]])]});
            var Q2;
            Q2=makeQuery(id+"F37.imprint","IMPRINT",FACE,{"disambiguationData":[TD([[makeQuery(id+"F37.imprint","IMPRINT",EDGE,{"derivedFrom":sQuery(id+"F37.wireOp",EDGE,"E95")}),1.0]])]});
            var Q3;
            Q3=makeQuery(id+"F37.imprint","IMPRINT",FACE,{"disambiguationData":[TD([[makeQuery(id+"F37.imprint","IMPRINT",EDGE,{"derivedFrom":sQuery(id+"F37.wireOp",EDGE,"E96")}),1.0]])]});
            var Q4;
            Q4=makeQuery(id+"F37.imprint","IMPRINT",FACE,{"disambiguationData":[TD([[makeQuery(id+"F37.imprint","IMPRINT",EDGE,{"derivedFrom":sQuery(id+"F37.wireOp",EDGE,"E97")}),1.0]])]});
            var Q5;
            Q5=makeQuery(id+"F37.imprint","IMPRINT",FACE,{"disambiguationData":[TD([[makeQuery(id+"F37.imprint","IMPRINT",EDGE,{"derivedFrom":sQuery(id+"F37.wireOp",EDGE,"E98")}),1.0]])]});
            var Q6;
            Q6=makeQuery(id+"F37.imprint","IMPRINT",FACE,{"disambiguationData":[TD([[makeQuery(id+"F37.imprint","IMPRINT",EDGE,{"derivedFrom":sQuery(id+"F37.wireOp",EDGE,"E99")}),1.0]])]});
            var Q7;
            Q7=makeQuery(id+"F37.imprint","IMPRINT",FACE,{"disambiguationData":[TD([[makeQuery(id+"F37.imprint","IMPRINT",EDGE,{"derivedFrom":sQuery(id+"F37.wireOp",EDGE,"E100")}),1.0]])]});
            var Q8;
            Q8=makeQuery(id+"F37.imprint","IMPRINT",FACE,{"disambiguationData":[TD([[makeQuery(id+"F37.imprint","IMPRINT",EDGE,{"derivedFrom":sQuery(id+"F37.wireOp",EDGE,"E101")}),1.0]])]});
            var Q9;
            Q9=makeQuery(id+"F37.imprint","IMPRINT",FACE,{"disambiguationData":[TD([[makeQuery(id+"F37.imprint","IMPRINT",EDGE,{"derivedFrom":sQuery(id+"F37.wireOp",EDGE,"E110")}),1.0]])]});
            var Q10;
            Q10=makeQuery(id+"F37.imprint","IMPRINT",FACE,{"disambiguationData":[TD([[makeQuery(id+"F37.imprint","IMPRINT",EDGE,{"derivedFrom":sQuery(id+"F37.wireOp",EDGE,"E109")}),1.0]])]});
            var Q11;
            Q11=makeQuery(id+"F37.imprint","IMPRINT",FACE,{"disambiguationData":[TD([[makeQuery(id+"F37.imprint","IMPRINT",EDGE,{"derivedFrom":sQuery(id+"F37.wireOp",EDGE,"E108")}),1.0]])]});
            var Q12;
            Q12=makeQuery(id+"F37.imprint","IMPRINT",FACE,{"disambiguationData":[TD([[makeQuery(id+"F37.imprint","IMPRINT",EDGE,{"derivedFrom":sQuery(id+"F37.wireOp",EDGE,"E107")}),1.0]])]});
            var Q13;
            Q13=makeQuery(id+"F37.imprint","IMPRINT",FACE,{"disambiguationData":[TD([[makeQuery(id+"F37.imprint","IMPRINT",EDGE,{"derivedFrom":sQuery(id+"F37.wireOp",EDGE,"E106")}),1.0]])]});
            var Q14;
            Q14=makeQuery(id+"F37.imprint","IMPRINT",FACE,{"disambiguationData":[TD([[makeQuery(id+"F37.imprint","IMPRINT",EDGE,{"derivedFrom":sQuery(id+"F37.wireOp",EDGE,"E105")}),1.0]])]});
            var Q15;
            Q15=makeQuery(id+"F37.imprint","IMPRINT",FACE,{"disambiguationData":[TD([[makeQuery(id+"F37.imprint","IMPRINT",EDGE,{"derivedFrom":sQuery(id+"F37.wireOp",EDGE,"E102")}),1.0]])]});
            var Q16;
            Q16=makeQuery(id+"F37.imprint","IMPRINT",FACE,{"disambiguationData":[TD([[makeQuery(id+"F37.imprint","IMPRINT",EDGE,{"derivedFrom":sQuery(id+"F37.wireOp",EDGE,"E103")}),1.0]])]});
            var Q17;
            Q17=makeQuery(id+"F37.imprint","IMPRINT",FACE,{"disambiguationData":[TD([[makeQuery(id+"F37.imprint","IMPRINT",EDGE,{"derivedFrom":sQuery(id+"F37.wireOp",EDGE,"E104")}),1.0]])]});
            var Q18;
            Q18=sQuery(id+"F37.wireOp",EDGE,"E102");
            var Q19;
            Q19=sQuery(id+"F37.wireOp",EDGE,"E103");
            var Q20;
            Q20=sQuery(id+"F37.wireOp",EDGE,"E104");
            var Q21;
            Q21=sQuery(id+"F37.wireOp",EDGE,"E105");
            var Q22;
            Q22=sQuery(id+"F37.wireOp",EDGE,"E106");
            var Q23;
            Q23=sQuery(id+"F37.wireOp",EDGE,"E107");
            var Q24;
            Q24=sQuery(id+"F37.wireOp",EDGE,"E108");
            var Q25;
            Q25=sQuery(id+"F37.wireOp",EDGE,"E110");
            var Q26;
            Q26=sQuery(id+"F37.wireOp",EDGE,"E109");
            var Q27;
            Q27=sQuery(id+"F37.wireOp",EDGE,"E101");
            var Q28;
            Q28=sQuery(id+"F37.wireOp",EDGE,"E100");
            var Q29;
            Q29=sQuery(id+"F37.wireOp",EDGE,"E99");
            var Q30;
            Q30=sQuery(id+"F37.wireOp",EDGE,"E98");
            var Q31;
            Q31=sQuery(id+"F37.wireOp",EDGE,"E97");
            var Q32;
            Q32=sQuery(id+"F37.wireOp",EDGE,"E96");
            var Q33;
            Q33=sQuery(id+"F37.wireOp",EDGE,"E95");
            var Q34;
            Q34=sQuery(id+"F37.wireOp",EDGE,"E94");
            var Q35;
            Q35=sQuery(id+"F37.wireOp",EDGE,"E93");
            extrude(context, id + "F38", {"entities" : qUnion([Q0, Q1, Q2, Q3, Q4, Q5, Q6, Q7, Q8, Q9, Q10, Q11, Q12, Q13, Q14, Q15, Q16, Q17]), "surfaceEntities" : qUnion([Q18, Q19, Q20, Q21, Q22, Q23, Q24, Q25, Q26, Q27, Q28, Q29, Q30, Q31, Q32, Q33, Q34, Q35]), "oppositeDirection" : true, "depth" : 15 * mm});
        }
        {
            var Q0;
            Q0=makeQuery(id+"F28.opExtrude","SWEPT_FACE",FACE,{"disambiguationData":[OSD([sQuery(id+"F27.wireOp",EDGE,"E73")])]});
            var sketch = newSketch(context, id + "F39", { "sketchPlane" : qUnion([Q0])});
            skLineSegment(sketch, "E111.bottom", {"start": v(163.6, 244.47) * mm, "end": v(189, 244.47) * mm});
            skLineSegment(sketch, "E111.top", {"start": v(163.6, 200.02) * mm, "end": v(189, 200.02) * mm});
            skLineSegment(sketch, "E111.left", {"start": v(163.6, 244.47) * mm, "end": v(163.6, 200.02) * mm});
            skLineSegment(sketch, "E111.right", {"start": v(189, 244.47) * mm, "end": v(189, 200.02) * mm});
            skLineSegment(sketch, "E112.bottom", {"start": v(-310.8, 244.47) * mm, "end": v(-285.4, 244.47) * mm});
            skLineSegment(sketch, "E112.top", {"start": v(-310.8, 200.02) * mm, "end": v(-285.4, 200.02) * mm});
            skLineSegment(sketch, "E112.left", {"start": v(-310.8, 244.47) * mm, "end": v(-310.8, 200.02) * mm});
            skLineSegment(sketch, "E112.right", {"start": v(-285.4, 244.47) * mm, "end": v(-285.4, 200.02) * mm});
            skSolve(sketch);
        }
        {
            var Q0;
            Q0=makeQuery(id+"F39.imprint","IMPRINT",FACE,{"disambiguationData":[TD([[makeQuery(id+"F39.imprint","IMPRINT",EDGE,{"derivedFrom":sQuery(id+"F39.wireOp",EDGE,"E112.bottom")}),-1.0]])]});
            var Q1;
            {var subQ0=sQuery(id+"F39.wireOp",EDGE,"E111.left");Q1=makeQuery(id+"F39.imprint","IMPRINT",FACE,{"disambiguationData":[TD([[makeQuery(id+"F39.imprint","IMPRINT",EDGE,{"derivedFrom":subQ0}),1.0]])]});}
            var Q2;
            {var subQ0=sQuery(id+"F39.wireOp",EDGE,"E111.right");Q2=makeQuery(id+"F39.imprint","IMPRINT",FACE,{"disambiguationData":[TD([[makeQuery(id+"F39.imprint","IMPRINT",EDGE,{"derivedFrom":subQ0}),-1.0]])]});}
            extrude(context, id + "F40", {"entities" : qUnion([Q0, Q1, Q2]), "operationType" : NewBodyOperationType.ADD, "depth" : 44.45 * mm});
        }
        {
            var Q0;
            Q0=makeQuery(id+"F40.opExtrude","SWEPT_FACE",FACE,{"disambiguationData":[OSD([sQuery(id+"F39.wireOp",EDGE,"E111.right")])]});
            var sketch = newSketch(context, id + "F41", { "sketchPlane" : qUnion([Q0])});
            skCircle(sketch, "E113", {"center": v(-520.2, 222.25) * mm, "radius": 5 * mm});
            skCircle(sketch, "E114", {"center": v(-520.2, 222.25) * mm, "radius": 8 * mm});
            skSolve(sketch);
        }
        {
            var Q0;
            Q0=makeQuery(id+"F41.imprint","IMPRINT",FACE,{"disambiguationData":[TD([[makeQuery(id+"F41.imprint","IMPRINT",EDGE,{"derivedFrom":sQuery(id+"F41.wireOp",EDGE,"E113")}),-1.0]])]});
            var Q1;
            Q1=makeQuery(id+"F41.imprint","IMPRINT",FACE,{"disambiguationData":[TD([[makeQuery(id+"F41.imprint","IMPRINT",EDGE,{"derivedFrom":sQuery(id+"F41.wireOp",EDGE,"E113")}),1.0]])]});
            extrude(context, id + "F42", {"entities" : qUnion([Q0, Q1]), "oppositeDirection" : true, "depth" : 480 * mm});
        }
        {
            var Q0;
            Q0=makeQuery(id+"F41.imprint","IMPRINT",FACE,{"disambiguationData":[TD([[makeQuery(id+"F41.imprint","IMPRINT",EDGE,{"derivedFrom":sQuery(id+"F41.wireOp",EDGE,"E113")}),1.0]])]});
            extrude(context, id + "F43", {"entities" : qUnion([Q0]), "oppositeDirection" : true, "depth" : 511 * mm, "hasSecondDirection" : true, "secondDirectionOppositeDirection" : false, "secondDirectionDepth" : 39 * mm});
        }
        {
            var Q0;
            Q0=makeQuery(id+"F28.opExtrude","SWEPT_FACE",FACE,{"disambiguationData":[OSD([sQuery(id+"F27.wireOp",EDGE,"E73")])]});
            var sketch = newSketch(context, id + "F44", { "sketchPlane" : qUnion([Q0])});
            skLineSegment(sketch, "E115.bottom", {"start": v(208, 234.95) * mm, "end": v(223, 234.95) * mm});
            skLineSegment(sketch, "E115.top", {"start": v(208, 209.55) * mm, "end": v(223, 209.55) * mm});
            skLineSegment(sketch, "E115.left", {"start": v(208, 234.95) * mm, "end": v(208, 209.55) * mm});
            skLineSegment(sketch, "E115.right", {"start": v(223, 234.95) * mm, "end": v(223, 209.55) * mm});
            skSolve(sketch);
        }
        {
            var Q0;
            Q0=makeQuery(id+"F44.imprint","IMPRINT",FACE,{"disambiguationData":[TD([[makeQuery(id+"F44.imprint","IMPRINT",EDGE,{"derivedFrom":sQuery(id+"F44.wireOp",EDGE,"E115.bottom")}),-1.0]])]});
            extrude(context, id + "F45", {"entities" : qUnion([Q0]), "operationType" : NewBodyOperationType.REMOVE, "oppositeDirection" : true, "depth" : 5 * mm});
        }
        {
            var Q0;
            Q0=makeQuery(id+"F32.opExtrude","SWEPT_FACE",FACE,{"disambiguationData":[OSD([sQuery(id+"F31.wireOp",EDGE,"E83")])]});
            var sketch = newSketch(context, id + "F46", { "sketchPlane" : qUnion([Q0])});
            skLineSegment(sketch, "E116.bottom", {"start": v(-556.2, 298.45) * mm, "end": v(-497.46, 298.45) * mm});
            skLineSegment(sketch, "E116.top", {"start": v(-556.2, 295.27) * mm, "end": v(-497.46, 295.27) * mm});
            skLineSegment(sketch, "E116.left", {"start": v(-556.2, 298.45) * mm, "end": v(-556.2, 295.27) * mm});
            skLineSegment(sketch, "E116.right", {"start": v(-497.46, 298.45) * mm, "end": v(-497.46, 295.27) * mm});
            skLineSegment(sketch, "E117.bottom", {"start": v(-556.2, 146.05) * mm, "end": v(-496.43, 146.05) * mm});
            skLineSegment(sketch, "E117.top", {"start": v(-556.2, 149.22) * mm, "end": v(-496.43, 149.22) * mm});
            skLineSegment(sketch, "E117.left", {"start": v(-556.2, 146.05) * mm, "end": v(-556.2, 149.22) * mm});
            skLineSegment(sketch, "E117.right", {"start": v(-496.43, 146.05) * mm, "end": v(-496.43, 149.22) * mm});
            skSolve(sketch);
        }
        {
            var Q0;
            Q0 = qSketchRegion(id + "F46", true);
            extrude(context, id + "F47", {"entities" : qUnion([Q0]), "operationType" : NewBodyOperationType.ADD, "depth" : 560 * mm});
        }
    });
